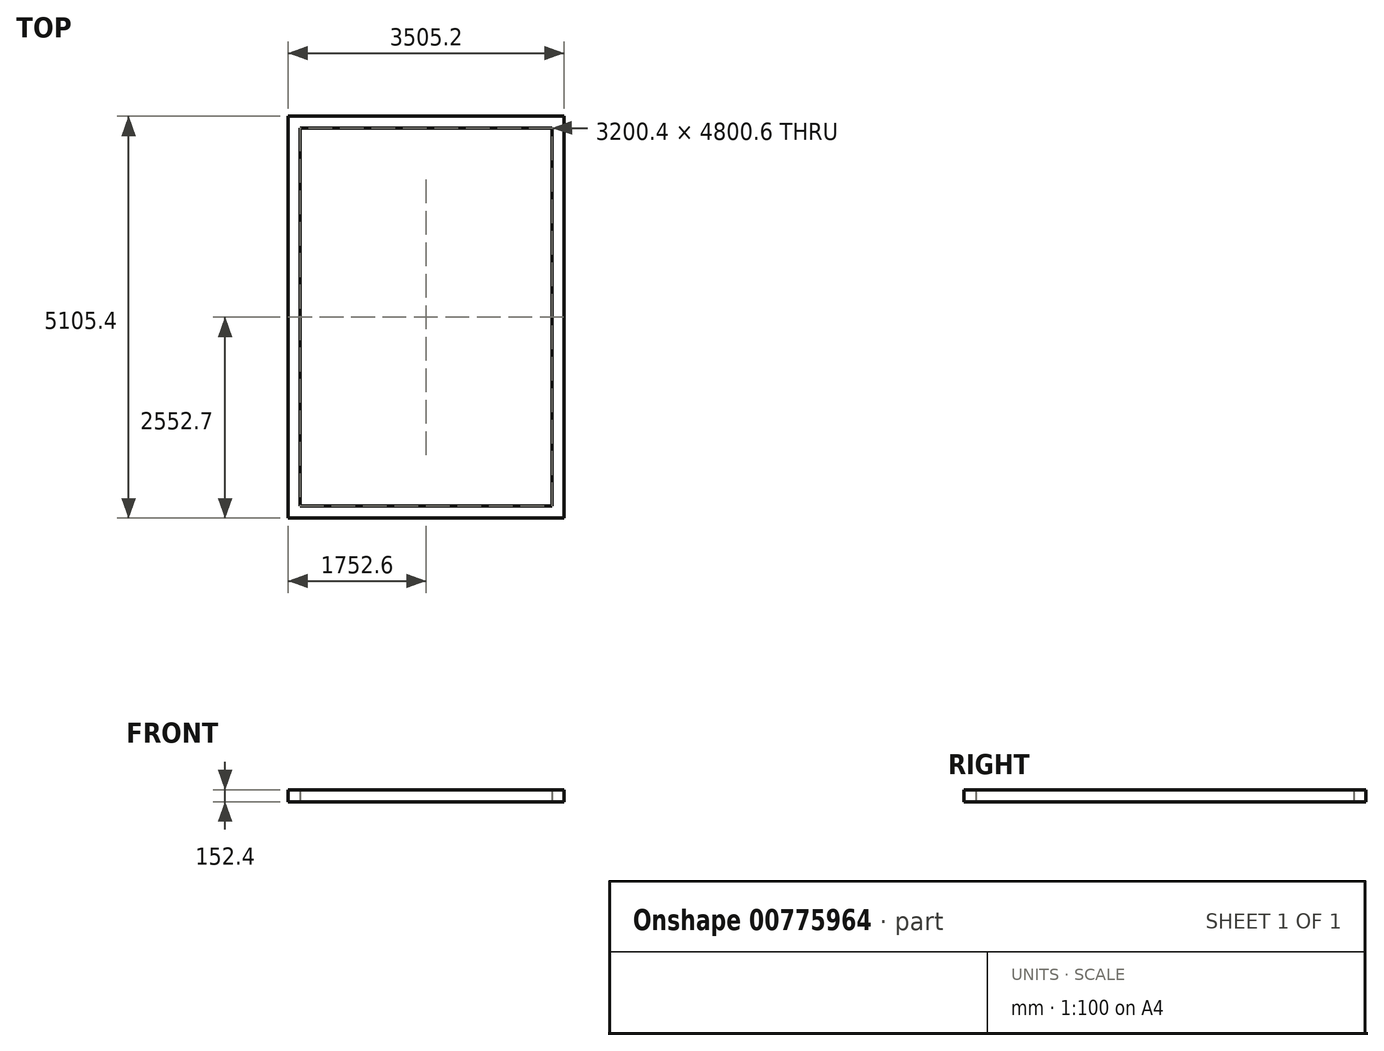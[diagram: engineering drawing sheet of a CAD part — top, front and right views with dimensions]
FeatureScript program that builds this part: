
annotation { "Feature Type Name" : "Feature", "Feature Type Description" : "" }
export const myFeature = defineFeature(function(context is Context, id is Id, definition is map)
    precondition{}
    {
        {
            var Q0;
            Q0=qCreatedBy(makeId("Top.planeOp"),FACE);
            var sketch = newSketch(context, id + "F0", { "sketchPlane" : qUnion([Q0])});
            skLineSegment(sketch, "E0.bottom", {"start": v(-1515.6, 2452.63) * mm, "end": v(1684.8, 2452.63) * mm});
            skLineSegment(sketch, "E0.top", {"start": v(-1515.6, -2347.97) * mm, "end": v(1684.8, -2347.97) * mm});
            skLineSegment(sketch, "E0.left", {"start": v(-1515.6, 2452.63) * mm, "end": v(-1515.6, -2347.97) * mm});
            skLineSegment(sketch, "E0.right", {"start": v(1684.8, 2452.63) * mm, "end": v(1684.8, -2347.97) * mm});
            skLineSegment(sketch, "E1.bottom", {"start": v(-1668, 2605.03) * mm, "end": v(1837.2, 2605.03) * mm});
            skLineSegment(sketch, "E1.top", {"start": v(-1668, -2500.37) * mm, "end": v(1837.2, -2500.37) * mm});
            skLineSegment(sketch, "E1.left", {"start": v(-1668, 2605.03) * mm, "end": v(-1668, -2500.37) * mm});
            skLineSegment(sketch, "E1.right", {"start": v(1837.2, 2605.03) * mm, "end": v(1837.2, -2500.37) * mm});
            skSolve(sketch);
        }
        {
            var Q0;
            Q0 = qSketchRegion(id + "F0", true);
            extrude(context, id + "F1", {"entities" : qUnion([Q0]), "depth" : 152.4 * mm, "offsetDistance" : 25.4 * mm});
        }
    });
